# Revit family: LEGRAND_TOMAS SIN ENCLAVAMIENTO_EMPOTRADAS_IP44_110
name_source: partatom
category: Installations électriques
revit_build: Autodesk Revit 2018 (Build: 20170223_1515(x64)
units: mm (PartAtom-declared; Revit-internal decimal feet)

## family parameters
Conserver l'orientation des annotations = Non
Cote de connecteur circulaire = Utiliser le diamètre
Couper avec des vides une fois chargée = Non
Hôte = Face
Partagée = Non
Point de calcul de pièce = Non
Type d'élément = Normal

## types (4) — shared parameters
Condiciones Generales de Uso = https://export.legrand.com
Description = Toma AL estándar internacional para montaje empotrado o en superficie con accesorio permite la alimentación de aparatos de potencia
Elévation par défaut = 1000 mm  [stored 3.28084 ft]
Estándar CEI o NFC = CEI
Fabricant = Legrand
Temperatura maxima de instalación = 40°C
Temperatura maxima de uso = 100°C
Temperatura minima de instalación = -20°C
Temperatura minima de uso = -50°C
Tension V = 110 V  50/60 Hz amarillo
clase de protección IP = IP44
color característico = amarillo
instalación de empotrar E o de superficie S = empotrar y superficie
numero de polos = 3
posición de la tierra h = 4
sin halogeno = Oui
tipo de conexión = conexión por tonillo

## per-type parameters (varying)
| type | Dia bouchon | Modèle | RAY BOUCHON | Ray | altura mm | ancho mm | distancia de fijación horizontal mm | distancia de fijación vertical mm | h1 | intensidad A | materia de la caja | profundidad de empotrar mm | profundidad mm | resistencia a los choques IK |
| base para cuadro entreejes unificados Hypra  IP44   16 A  110 V   2P+T  plast | 50 mm | 051919 | 25 mm  [stored 0.082021 ft] | 25 mm  [stored 0.082021 ft] | 84 mm | 84 mm | 70 mm | 70 mm | 50 mm | 16 A | plástico | 41 mm | 73 mm  [stored 0.239501 ft] | 09 |
| base para cuadro  Hypra  IP44   16 A  110 V   2P+T  plast | 50 mm | 051920 | 25 mm  [stored 0.082021 ft] | 25 mm  [stored 0.082021 ft] | 84 mm | 84 mm | 70 mm | 70 mm | 50 mm | 16 A | plástico | 41 mm | 81 mm | 09 |
| base para cuadro  Hypra  IP44   32 A  110 V   2P+T  plast | 50 mm | 051921 | 25 mm  [stored 0.082021 ft] | 25 mm  [stored 0.082021 ft] | 84 mm | 83 mm | 70 mm | 70 mm | 50 mm | 32 A | plástico | 50 mm | 103 mm | 09 |
| base para cuadro  Hypra  IP44   16 A  110 V   2P+T  métal | 38 mm | 051930 | 19 mm | 19 mm | 72 mm | 64 mm | 52 mm | 60 mm | 43 mm | 16 A | metal | 41 mm | 81 mm | 10 |

note: [stored X ft] marks values corroborated as IEEE doubles in the binary element streams (Revit-internal decimal feet)
